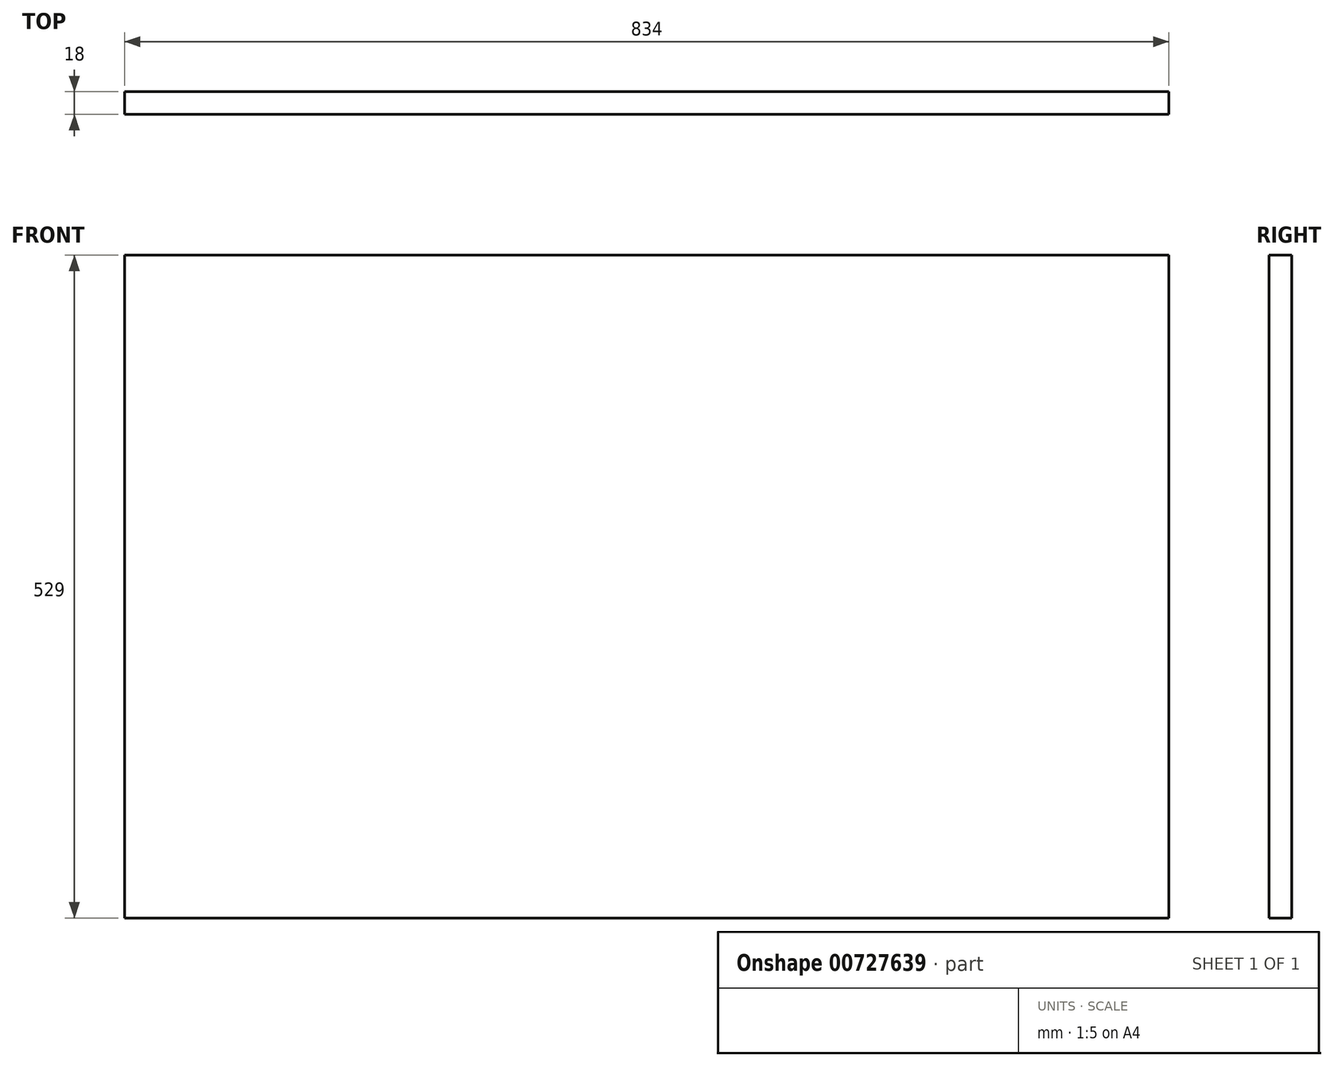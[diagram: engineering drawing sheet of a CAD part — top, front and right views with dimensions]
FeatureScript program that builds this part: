
annotation { "Feature Type Name" : "Feature", "Feature Type Description" : "" }
export const myFeature = defineFeature(function(context is Context, id is Id, definition is map)
    precondition{}
    {
        {
            var Q0;
            Q0=qCreatedBy(makeId("Front.planeOp"),FACE);
            var sketch = newSketch(context, id + "F0", { "sketchPlane" : qUnion([Q0])});
            skLineSegment(sketch, "E0.bottom", {"start": v(-417, 264.5) * mm, "end": v(417, 264.5) * mm});
            skLineSegment(sketch, "E0.top", {"start": v(-417, -264.5) * mm, "end": v(417, -264.5) * mm});
            skLineSegment(sketch, "E0.left", {"start": v(-417, 264.5) * mm, "end": v(-417, -264.5) * mm});
            skLineSegment(sketch, "E0.right", {"start": v(417, 264.5) * mm, "end": v(417, -264.5) * mm});
            skLineSegment(sketch, "E1", {"start": v(-417, 264.5) * mm, "end": v(417, -264.5) * mm, "construction": true});
            skSolve(sketch);
        }
        {
            var Q0;
            Q0 = qSketchRegion(id + "F0", true);
            extrude(context, id + "F1", {"entities" : qUnion([Q0]), "depth" : 18 * mm, "offsetDistance" : 25 * mm});
        }
    });
